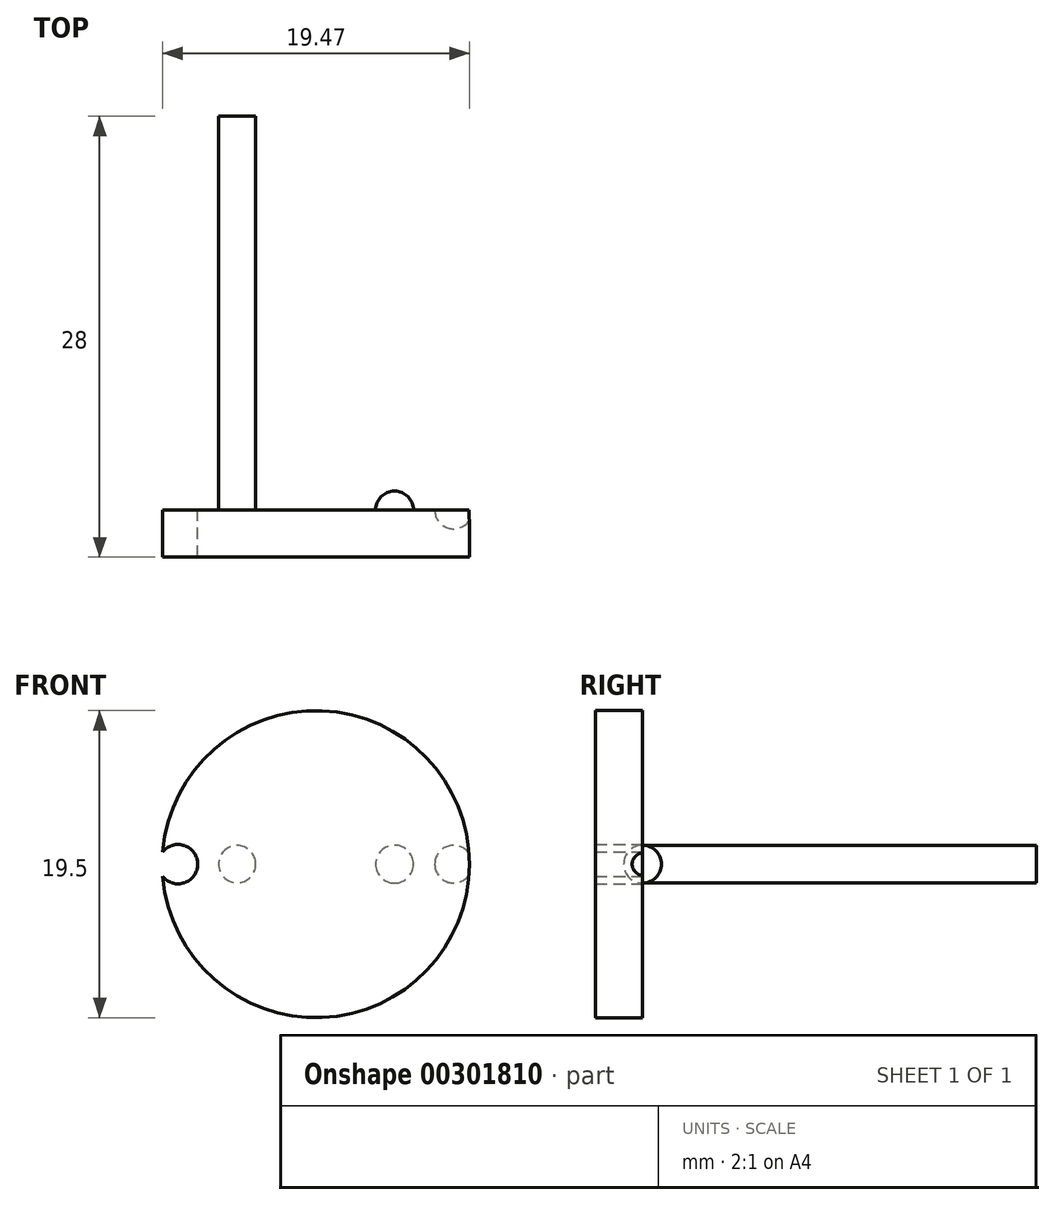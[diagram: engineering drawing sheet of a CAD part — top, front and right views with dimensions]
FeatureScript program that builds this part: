
annotation { "Feature Type Name" : "Feature", "Feature Type Description" : "" }
export const myFeature = defineFeature(function(context is Context, id is Id, definition is map)
    precondition{}
    {
        {
            var Q0;
            Q0=qCreatedBy(makeId("Front.planeOp"),FACE);
            var sketch = newSketch(context, id + "F0", { "sketchPlane" : qUnion([Q0])});
            skCircle(sketch, "E0", {"center": v(0, 0) * mm, "radius": 9.75 * mm});
            skSolve(sketch);
        }
        {
            var Q0;
            Q0 = qSketchRegion(id + "F0", true);
            extrude(context, id + "F1", {"entities" : qUnion([Q0]), "depth" : 3 * mm});
        }
        {
            var Q0;
            Q0=qCreatedBy(makeId("Top.planeOp"),FACE);
            var sketch = newSketch(context, id + "F2", { "sketchPlane" : qUnion([Q0])});
            skLineSegment(sketch, "E1", {"start": v(0, 0) * mm, "end": v(8.75, 0) * mm, "construction": true});
            skLineSegment(sketch, "E2", {"start": v(8.75, 0) * mm, "end": v(8.75, 6.32) * mm, "construction": true});
            skArc(sketch, "E3", {"start": v(9.95, 0) * mm, "mid": v(8.75, 1.2) * mm, "end": v(7.55, 0) * mm});
            skLineSegment(sketch, "E4", {"start": v(7.55, 0) * mm, "end": v(9.95, 0) * mm});
            skSolve(sketch);
        }
        {
            var Q0;
            Q0 = qSketchRegion(id + "F2", true);
            var Q1;
            Q1=sQuery(id+"F2.wireOp",EDGE,"E1");
            revolve(context, id + "F3", {"operationType" : NewBodyOperationType.ADD, "entities" : qUnion([Q0]), "axis" : qUnion([Q1]), "revolveType" : RevolveType.FULL});
        }
        {
            var Q0;
            Q0=qCreatedBy(makeId("Top.planeOp"),FACE);
            var sketch = newSketch(context, id + "F4", { "sketchPlane" : qUnion([Q0])});
            skLineSegment(sketch, "E5", {"start": v(0, 0) * mm, "end": v(5, 0) * mm, "construction": true});
            skLineSegment(sketch, "E6", {"start": v(5, 0) * mm, "end": v(5, 4.86) * mm, "construction": true});
            skArc(sketch, "E7", {"start": v(6.2, 0) * mm, "mid": v(5, 1.2) * mm, "end": v(3.8, 0) * mm});
            skLineSegment(sketch, "E8", {"start": v(3.8, 0) * mm, "end": v(6.2, 0) * mm});
            skSolve(sketch);
        }
        {
            var Q0;
            Q0 = qSketchRegion(id + "F4", true);
            var Q1;
            Q1=sQuery(id+"F4.wireOp",EDGE,"E5");
            revolve(context, id + "F5", {"operationType" : NewBodyOperationType.ADD, "entities" : qUnion([Q0]), "axis" : qUnion([Q1]), "revolveType" : RevolveType.FULL});
        }
        {
            var Q0;
            Q0=qCreatedBy(makeId("Front.planeOp"),FACE);
            var sketch = newSketch(context, id + "F6", { "sketchPlane" : qUnion([Q0])});
            skCircle(sketch, "E9", {"center": v(-5, 0) * mm, "radius": 1.18 * mm});
            skSolve(sketch);
        }
        {
            var Q0;
            Q0 = qSketchRegion(id + "F6", true);
            extrude(context, id + "F7", {"entities" : qUnion([Q0]), "operationType" : NewBodyOperationType.ADD, "oppositeDirection" : true, "depth" : 25 * mm});
        }
        {
            var Q0;
            Q0=makeQuery(id+"F1.opExtrude","CAP_FACE",FACE,{"disambiguationData":[OSD([sQuery(id+"F0.wireOp",EDGE,"E0")])],"isStart":true});
            var sketch = newSketch(context, id + "F8", { "sketchPlane" : qUnion([Q0])});
            skLineSegment(sketch, "E10", {"start": v(0, 0) * mm, "end": v(8.75, 0) * mm, "construction": true});
            skCircle(sketch, "E11", {"center": v(8.75, 0) * mm, "radius": 1.25 * mm});
            skSolve(sketch);
        }
        {
            var Q0;
            Q0 = qSketchRegion(id + "F8", true);
            extrude(context, id + "F9", {"entities" : qUnion([Q0]), "operationType" : NewBodyOperationType.REMOVE, "endBound" : BoundingType.UP_TO_NEXT, "oppositeDirection" : true, "depth" : 25 * mm});
        }
    });
